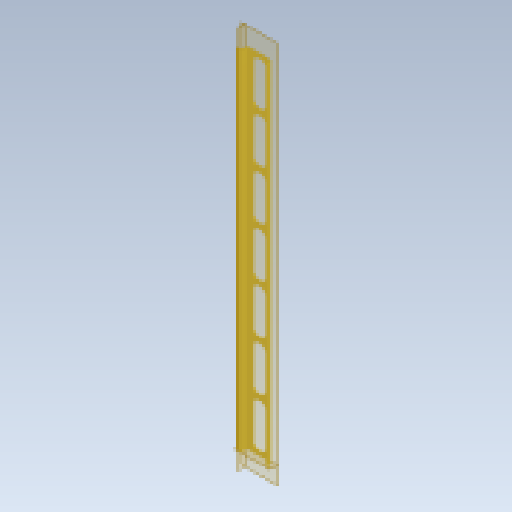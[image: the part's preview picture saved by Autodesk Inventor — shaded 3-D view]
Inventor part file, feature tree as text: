
AUTODESK INVENTOR PART (.ipt)
format: ipt  version: 2025.2 (Build 292293000, 293)  size: 192,000 bytes
history: native  units: mm
features: extrude x2, sketch x2, pattern_linear x1
ambient origin geometry x8: Origin, YZ Plane, XZ Plane, XY Plane, X Axis, Y Axis, Z Axis, Center Point
bodies: Solid1 (feature_tree)
feature tree (5):
  extrude  "Extrusion1"  Depth=159.0mm TaperAngle=0.0deg
  extrude  "Extrusion2"  Depth=2.95mm
  pattern_linear  "Rectangular Pattern1"  Spacing1=10.0mm  [1 undecoded]
  sketch  "Sketch_2"  dims[d0=159.0mm d1=0.0mm d2=2.0mm d3=0.0mm]
  sketch  "Sketch_6"  dims[d4=800.0mm d6=22.6mm d7=10.0mm d9=0.0mm d13=2.95mm d14=10.0mm]
note: 1 required parameter value undecoded (feature->parameter linkage not recoverable at this tier; creation-order binding heuristic only, values carry confidence <= 0.55)
